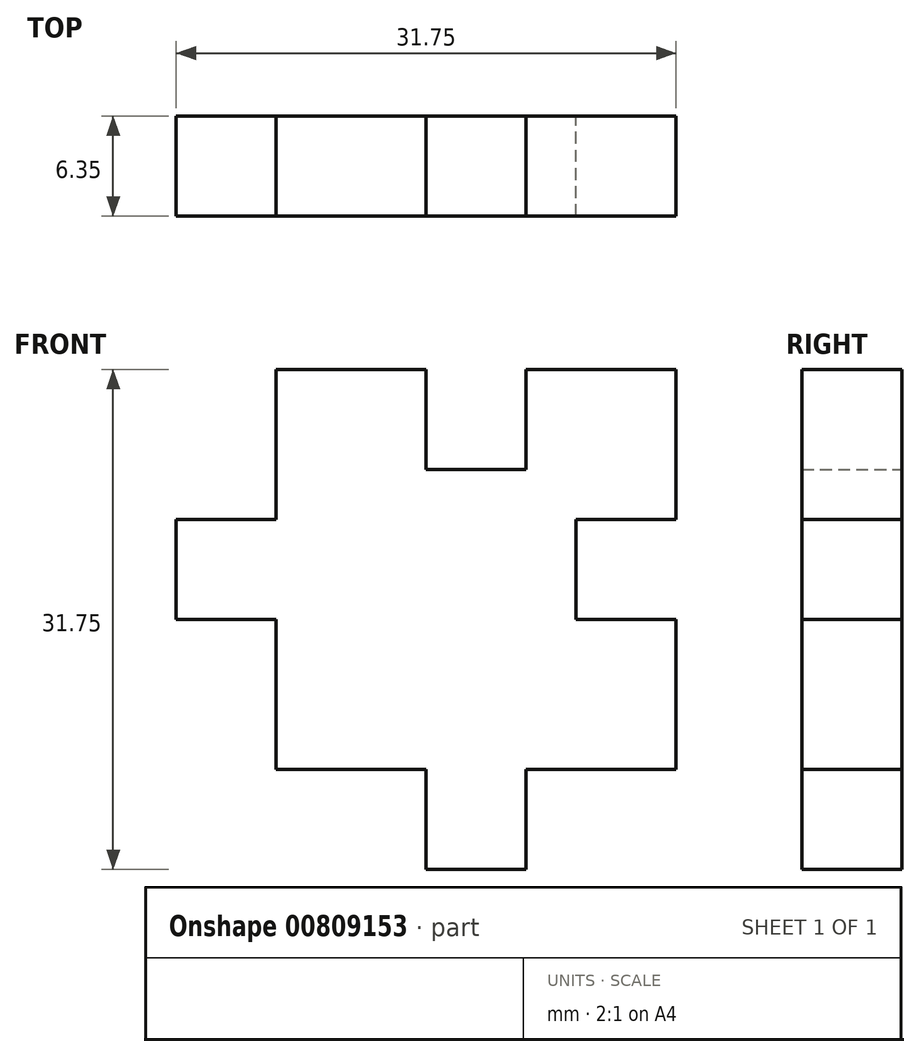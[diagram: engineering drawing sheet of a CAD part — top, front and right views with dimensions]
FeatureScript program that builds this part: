
annotation { "Feature Type Name" : "Feature", "Feature Type Description" : "" }
export const myFeature = defineFeature(function(context is Context, id is Id, definition is map)
    precondition{}
    {
        {
            var Q0;
            Q0=qCreatedBy(makeId("Front.planeOp"),FACE);
            var sketch = newSketch(context, id + "F0", { "sketchPlane" : qUnion([Q0])});
            skLineSegment(sketch, "E0", {"start": v(0, 0) * mm, "end": v(0, 6.35) * mm});
            skLineSegment(sketch, "E1", {"start": v(-3.18, 12.7) * mm, "end": v(-12.7, 12.7) * mm});
            skLineSegment(sketch, "E2", {"start": v(-12.7, 12.7) * mm, "end": v(-12.7, 3.17) * mm});
            skLineSegment(sketch, "E3", {"start": v(-12.7, -12.7) * mm, "end": v(-3.17, -12.7) * mm});
            skLineSegment(sketch, "E4", {"start": v(12.7, -12.7) * mm, "end": v(12.7, -3.18) * mm});
            skLineSegment(sketch, "E5", {"start": v(3.18, 12.7) * mm, "end": v(12.7, 12.7) * mm});
            skLineSegment(sketch, "E6", {"start": v(-3.18, 12.7) * mm, "end": v(-3.18, 6.35) * mm});
            skPoint(sketch, "E6.endSnap0", {"position": v(0, 6.35) * mm});
            skLineSegment(sketch, "E7", {"start": v(3.18, 12.7) * mm, "end": v(3.18, 6.35) * mm});
            skLineSegment(sketch, "E8", {"start": v(-3.18, 6.35) * mm, "end": v(3.18, 6.35) * mm});
            skPoint(sketch, "E9.orphan", {"position": v(0, 12.7) * mm});
            skLineSegment(sketch, "E10", {"start": v(-19.05, 3.17) * mm, "end": v(-12.7, 3.17) * mm});
            skLineSegment(sketch, "E11", {"start": v(-19.05, 3.17) * mm, "end": v(-19.05, -3.18) * mm});
            skLineSegment(sketch, "E12", {"start": v(-12.7, -3.18) * mm, "end": v(-19.05, -3.18) * mm});
            skLineSegment(sketch, "E13.trimOffspring", {"start": v(-12.7, -3.18) * mm, "end": v(-12.7, -12.7) * mm});
            skPoint(sketch, "E14.end.orphan", {"position": v(-12.7, 0) * mm});
            skLineSegment(sketch, "E15", {"start": v(-3.18, -12.7) * mm, "end": v(-3.18, -19.05) * mm});
            skLineSegment(sketch, "E16", {"start": v(-3.18, -19.05) * mm, "end": v(-3.18, -12.7) * mm});
            skLineSegment(sketch, "E17", {"start": v(-3.18, -19.05) * mm, "end": v(3.17, -19.05) * mm});
            skLineSegment(sketch, "E18", {"start": v(3.17, -12.7) * mm, "end": v(3.17, -19.05) * mm});
            skLineSegment(sketch, "E19.trimOffspring", {"start": v(3.17, -12.7) * mm, "end": v(12.7, -12.7) * mm});
            skPoint(sketch, "E20.end.orphan", {"position": v(0, -12.7) * mm});
            skLineSegment(sketch, "E21", {"start": v(12.7, 3.17) * mm, "end": v(6.35, 3.17) * mm});
            skLineSegment(sketch, "E22", {"start": v(6.35, 3.17) * mm, "end": v(6.35, -3.18) * mm});
            skLineSegment(sketch, "E23", {"start": v(12.7, -3.18) * mm, "end": v(6.35, -3.18) * mm});
            skPoint(sketch, "E24.start.orphan", {"position": v(12.7, 0) * mm});
            skLineSegment(sketch, "E25.trimOffspring", {"start": v(12.7, 3.17) * mm, "end": v(12.7, 12.7) * mm});
            skSolve(sketch);
        }
        {
            var Q0;
            Q0=makeQuery(id+"F0.imprint","IMPRINT",FACE,{"disambiguationData":[TD([[makeQuery(id+"F0.imprint","IMPRINT",EDGE,{"derivedFrom":sQuery(id+"F0.wireOp",EDGE,"E1")}),1.0]])]});
            extrude(context, id + "F1", {"entities" : qUnion([Q0]), "depth" : 6.35 * mm, "offsetDistance" : 25.4 * mm});
        }
    });
